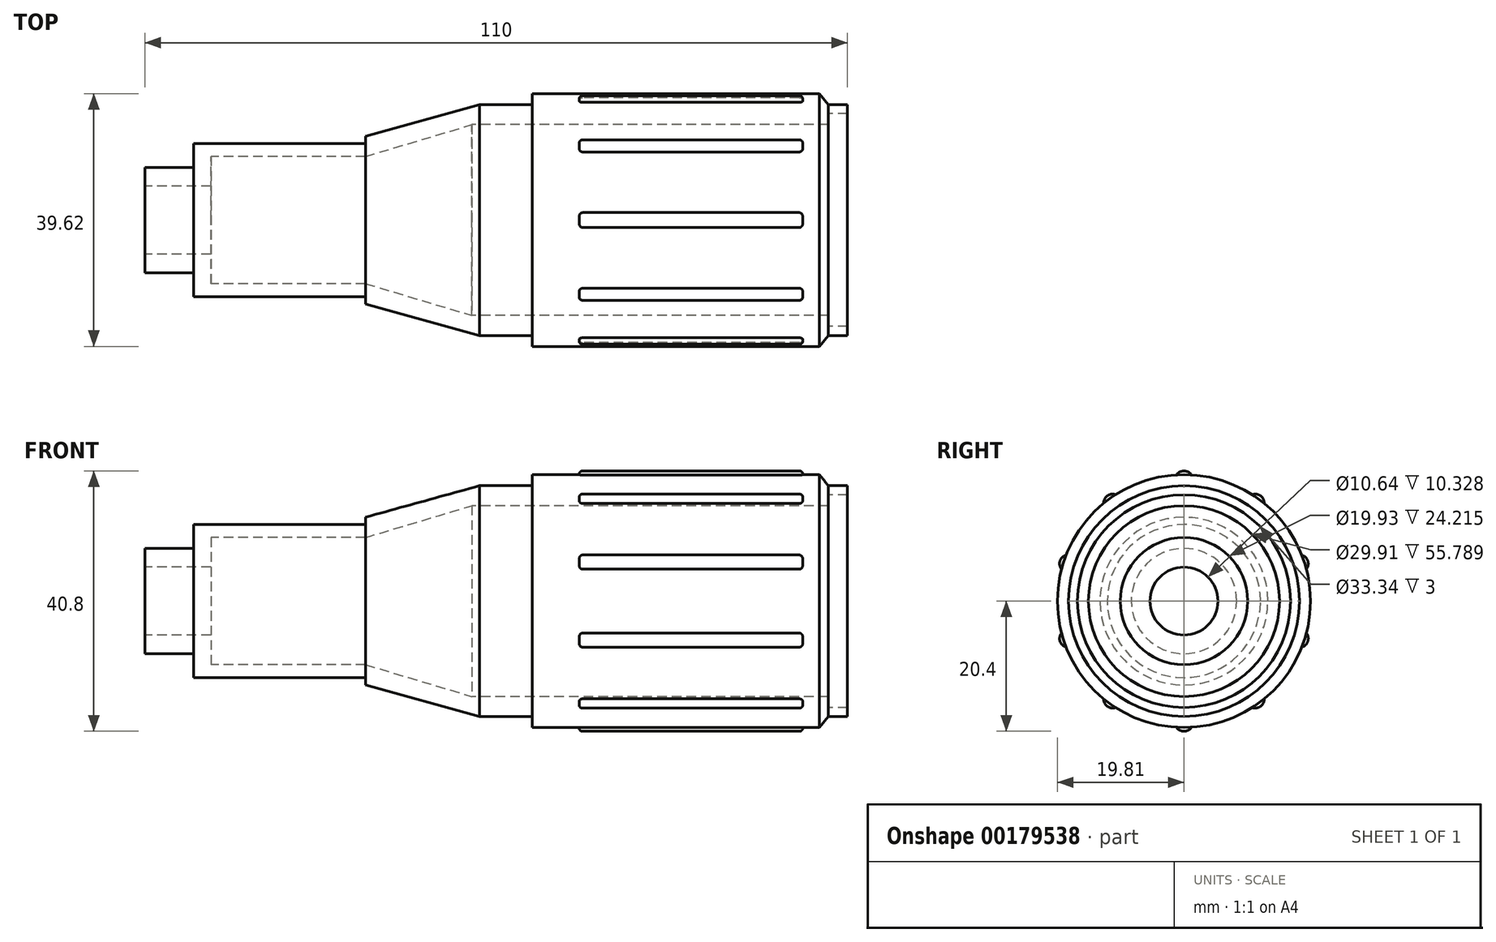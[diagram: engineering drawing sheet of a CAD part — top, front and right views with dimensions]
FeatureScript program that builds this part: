
annotation { "Feature Type Name" : "Feature", "Feature Type Description" : "" }
export const myFeature = defineFeature(function(context is Context, id is Id, definition is map)
    precondition{}
    {
        {
            var Q0;
            Q0=qCreatedBy(makeId("Front.planeOp"),FACE);
            var sketch = newSketch(context, id + "F0", { "sketchPlane" : qUnion([Q0])});
            skLineSegment(sketch, "E0", {"start": v(0, 5.32) * mm, "end": v(0, 8.25) * mm});
            skLineSegment(sketch, "E1", {"start": v(0, 8.25) * mm, "end": v(7.63, 8.25) * mm});
            skLineSegment(sketch, "E2", {"start": v(7.63, 8.25) * mm, "end": v(7.63, 12) * mm});
            skLineSegment(sketch, "E3", {"start": v(7.63, 12) * mm, "end": v(17.47, 12) * mm});
            skLineSegment(sketch, "E4", {"start": v(17.47, 12) * mm, "end": v(17.47, 12) * mm});
            skLineSegment(sketch, "E5", {"start": v(17.47, 12) * mm, "end": v(34.54, 12) * mm});
            skLineSegment(sketch, "E6", {"start": v(34.54, 12) * mm, "end": v(34.54, 13.14) * mm});
            skLineSegment(sketch, "E7", {"start": v(34.54, 13.14) * mm, "end": v(52.4, 18.08) * mm});
            skLineSegment(sketch, "E8", {"start": v(52.4, 18.08) * mm, "end": v(60.62, 18.08) * mm});
            skLineSegment(sketch, "E9", {"start": v(60.62, 18.08) * mm, "end": v(60.62, 19.81) * mm});
            skLineSegment(sketch, "E10", {"start": v(60.62, 19.81) * mm, "end": v(105.62, 19.81) * mm});
            skLineSegment(sketch, "E11", {"start": v(105.62, 19.81) * mm, "end": v(107, 18.08) * mm});
            skLineSegment(sketch, "E12", {"start": v(107, 18.08) * mm, "end": v(110, 18.08) * mm});
            skLineSegment(sketch, "E13", {"start": v(110, 18.08) * mm, "end": v(110, 16.67) * mm});
            skLineSegment(sketch, "E14", {"start": v(110, 16.67) * mm, "end": v(107, 16.67) * mm});
            skLineSegment(sketch, "E15", {"start": v(107, 16.67) * mm, "end": v(107, 14.96) * mm});
            skLineSegment(sketch, "E16", {"start": v(107, 14.96) * mm, "end": v(51.21, 14.96) * mm});
            skLineSegment(sketch, "E17", {"start": v(51.21, 14.96) * mm, "end": v(34.54, 9.96) * mm});
            skLineSegment(sketch, "E18", {"start": v(34.54, 9.96) * mm, "end": v(10.33, 9.96) * mm});
            skLineSegment(sketch, "E19", {"start": v(10.33, 9.96) * mm, "end": v(10.33, 5.32) * mm});
            skLineSegment(sketch, "E20", {"start": v(10.33, 5.32) * mm, "end": v(0, 5.32) * mm});
            skLineSegment(sketch, "E21", {"start": v(0, 0) * mm, "end": v(145.16, 0) * mm, "construction": true});
            skSolve(sketch);
        }
        {
            var Q0;
            Q0=makeQuery(id+"F0.imprint","IMPRINT",FACE,{"disambiguationData":[TD([[makeQuery(id+"F0.imprint","IMPRINT",EDGE,{"derivedFrom":sQuery(id+"F0.wireOp",EDGE,"E0")}),-1.0]])]});
            var Q1;
            Q1=sQuery(id+"F0.wireOp",EDGE,"E21");
            revolve(context, id + "F1", {"surfaceOperationType" : NewSurfaceOperationType.NEW, "entities" : qUnion([Q0]), "axis" : qUnion([Q1]), "revolveType" : RevolveType.FULL});
        }
        {
            var Q0;
            Q0=qCreatedBy(makeId("Right.planeOp"),FACE);
            cPlane(context, id + "F2", {"entities" : qUnion([Q0]), "cplaneType" : CPlaneType.OFFSET, "offset" : 68 * mm, "width" : 150 * mm, "height" : 150 * mm});
        }
        {
            var Q0;
            Q0=qCreatedBy(id+"F2.planeOp",FACE);
            var sketch = newSketch(context, id + "F3", { "sketchPlane" : qUnion([Q0])});
            skCircle(sketch, "E22", {"center": v(0, 19) * mm, "radius": 1.4 * mm});
            skCircle(sketch, "E23.1.0", {"center": v(-11.17, 15.37) * mm, "radius": 1.4 * mm});
            skCircle(sketch, "E23.2.0", {"center": v(-18.07, 5.87) * mm, "radius": 1.4 * mm});
            skCircle(sketch, "E23.3.0", {"center": v(-18.07, -5.87) * mm, "radius": 1.4 * mm});
            skCircle(sketch, "E23.4.0", {"center": v(-11.17, -15.37) * mm, "radius": 1.4 * mm});
            skCircle(sketch, "E23.5.0", {"center": v(0, -19) * mm, "radius": 1.4 * mm});
            skCircle(sketch, "E23.6.0", {"center": v(11.17, -15.37) * mm, "radius": 1.4 * mm});
            skCircle(sketch, "E23.7.0", {"center": v(18.07, -5.87) * mm, "radius": 1.4 * mm});
            skCircle(sketch, "E23.8.0", {"center": v(18.07, 5.87) * mm, "radius": 1.4 * mm});
            skCircle(sketch, "E23.9.0", {"center": v(11.17, 15.37) * mm, "radius": 1.4 * mm});
            skPoint(sketch, "E23.center", {"position": v(0, 0) * mm});
            skSolve(sketch);
        }
        {
            var Q0;
            Q0 = qSketchRegion(id + "F3", true);
            extrude(context, id + "F4", {"entities" : qUnion([Q0]), "operationType" : NewBodyOperationType.ADD, "depth" : 35 * mm, "offsetDistance" : 25 * mm});
        }
        {
            var Q0;
            Q0=makeQuery(id+"F4.opExtrude","CAP_EDGE",EDGE,{"disambiguationData":[OSD([sQuery(id+"F3.wireOp",EDGE,"E22")])],"isStart":false});
            var Q1;
            Q1=makeQuery(id+"F4.opExtrude","CAP_EDGE",EDGE,{"disambiguationData":[OSD([sQuery(id+"F3.wireOp",EDGE,"E23.9.0")])],"isStart":false});
            var Q2;
            Q2=makeQuery(id+"F4.opExtrude","CAP_EDGE",EDGE,{"disambiguationData":[OSD([sQuery(id+"F3.wireOp",EDGE,"E23.1.0")])],"isStart":false});
            var Q3;
            Q3=makeQuery(id+"F4.opExtrude","CAP_EDGE",EDGE,{"disambiguationData":[OSD([sQuery(id+"F3.wireOp",EDGE,"E23.2.0")])],"isStart":false});
            var Q4;
            Q4=makeQuery(id+"F4.opExtrude","CAP_EDGE",EDGE,{"disambiguationData":[OSD([sQuery(id+"F3.wireOp",EDGE,"E23.3.0")])],"isStart":false});
            var Q5;
            Q5=makeQuery(id+"F4.opExtrude","CAP_EDGE",EDGE,{"disambiguationData":[OSD([sQuery(id+"F3.wireOp",EDGE,"E23.4.0")])],"isStart":false});
            var Q6;
            Q6=makeQuery(id+"F4.opExtrude","CAP_EDGE",EDGE,{"disambiguationData":[OSD([sQuery(id+"F3.wireOp",EDGE,"E23.5.0")])],"isStart":false});
            var Q7;
            Q7=makeQuery(id+"F4.opExtrude","CAP_EDGE",EDGE,{"disambiguationData":[OSD([sQuery(id+"F3.wireOp",EDGE,"E23.6.0")])],"isStart":false});
            var Q8;
            Q8=makeQuery(id+"F4.opExtrude","CAP_EDGE",EDGE,{"disambiguationData":[OSD([sQuery(id+"F3.wireOp",EDGE,"E23.7.0")])],"isStart":false});
            var Q9;
            Q9=makeQuery(id+"F4.opExtrude","CAP_EDGE",EDGE,{"disambiguationData":[OSD([sQuery(id+"F3.wireOp",EDGE,"E23.8.0")])],"isStart":false});
            var Q10;
            Q10=makeQuery(id+"F4.opExtrude","CAP_EDGE",EDGE,{"disambiguationData":[OSD([sQuery(id+"F3.wireOp",EDGE,"E23.9.0")])],"isStart":true});
            var Q11;
            Q11=makeQuery(id+"F4.opExtrude","CAP_EDGE",EDGE,{"disambiguationData":[OSD([sQuery(id+"F3.wireOp",EDGE,"E23.8.0")])],"isStart":true});
            var Q12;
            Q12=makeQuery(id+"F4.opExtrude","CAP_EDGE",EDGE,{"disambiguationData":[OSD([sQuery(id+"F3.wireOp",EDGE,"E23.7.0")])],"isStart":true});
            var Q13;
            Q13=makeQuery(id+"F4.opExtrude","CAP_EDGE",EDGE,{"disambiguationData":[OSD([sQuery(id+"F3.wireOp",EDGE,"E23.6.0")])],"isStart":true});
            var Q14;
            Q14=makeQuery(id+"F4.opExtrude","CAP_EDGE",EDGE,{"disambiguationData":[OSD([sQuery(id+"F3.wireOp",EDGE,"E23.5.0")])],"isStart":true});
            var Q15;
            Q15=makeQuery(id+"F4.opExtrude","CAP_EDGE",EDGE,{"disambiguationData":[OSD([sQuery(id+"F3.wireOp",EDGE,"E23.4.0")])],"isStart":true});
            var Q16;
            Q16=makeQuery(id+"F4.opExtrude","CAP_EDGE",EDGE,{"disambiguationData":[OSD([sQuery(id+"F3.wireOp",EDGE,"E23.3.0")])],"isStart":true});
            var Q17;
            Q17=makeQuery(id+"F4.opExtrude","CAP_EDGE",EDGE,{"disambiguationData":[OSD([sQuery(id+"F3.wireOp",EDGE,"E22")])],"isStart":true});
            var Q18;
            Q18=makeQuery(id+"F4.opExtrude","CAP_EDGE",EDGE,{"disambiguationData":[OSD([sQuery(id+"F3.wireOp",EDGE,"E23.1.0")])],"isStart":true});
            var Q19;
            Q19=makeQuery(id+"F4.opExtrude","CAP_EDGE",EDGE,{"disambiguationData":[OSD([sQuery(id+"F3.wireOp",EDGE,"E23.2.0")])],"isStart":true});
            fillet(context, id + "F5", {"entities" : qUnion([Q0, Q1, Q2, Q3, Q4, Q5, Q6, Q7, Q8, Q9, Q10, Q11, Q12, Q13, Q14, Q15, Q16, Q17, Q18, Q19]), "radius" : 0.5 * mm, "tangentPropagation" : true, "allowEdgeOverflow" : false});
        }
    });
